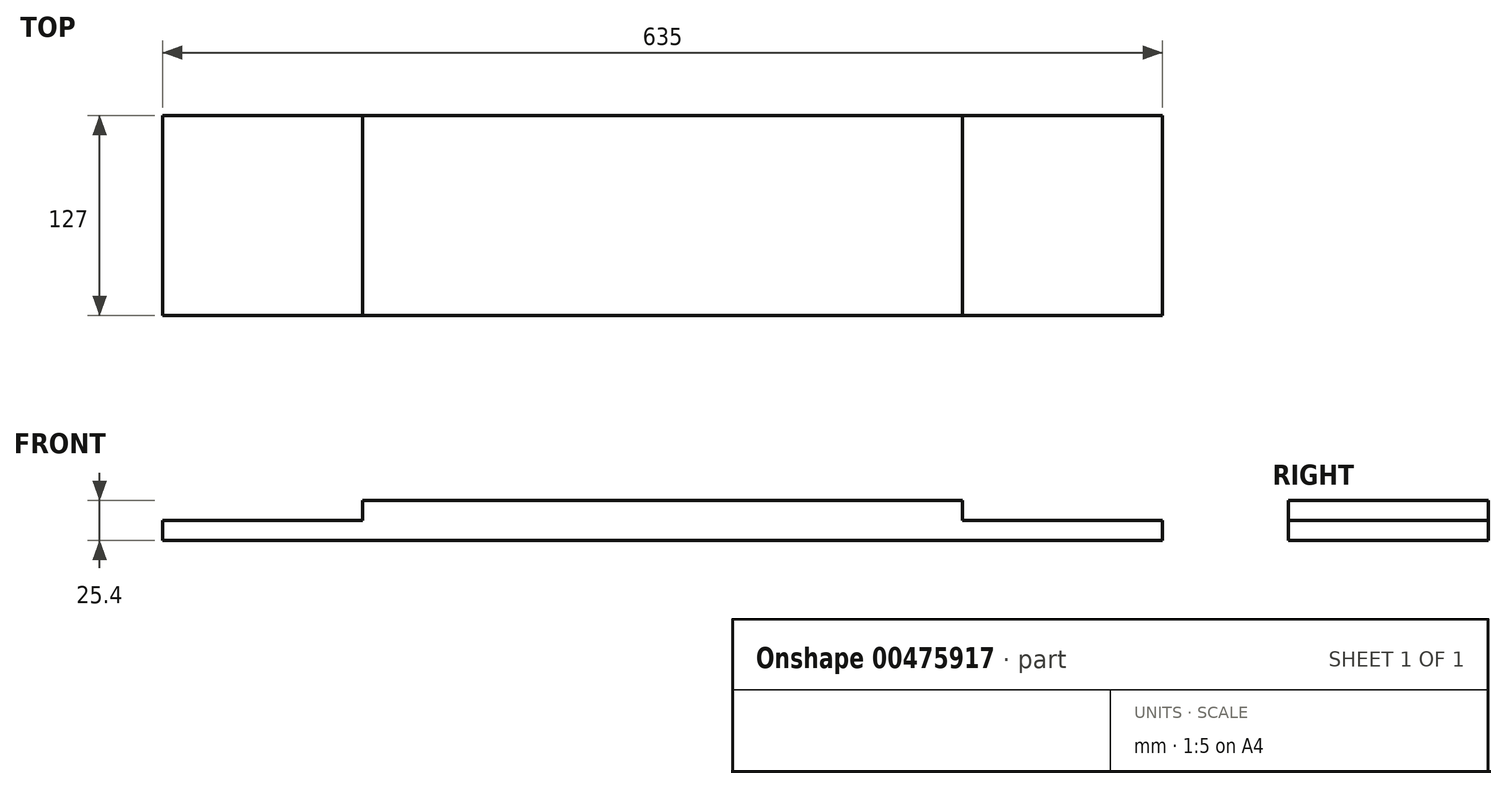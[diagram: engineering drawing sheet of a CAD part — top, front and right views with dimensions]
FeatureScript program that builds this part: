
annotation { "Feature Type Name" : "Feature", "Feature Type Description" : "" }
export const myFeature = defineFeature(function(context is Context, id is Id, definition is map)
    precondition{}
    {
        {
            var Q0;
            Q0=qCreatedBy(makeId("Top.planeOp"),FACE);
            var sketch = newSketch(context, id + "F0", { "sketchPlane" : qUnion([Q0])});
            skLineSegment(sketch, "E0.bottom", {"start": v(-183.86, -84.48) * mm, "end": v(197.14, -84.48) * mm});
            skLineSegment(sketch, "E0.top", {"start": v(-183.86, 42.52) * mm, "end": v(197.14, 42.52) * mm});
            skLineSegment(sketch, "E0.left", {"start": v(-183.86, -84.48) * mm, "end": v(-183.86, 42.52) * mm});
            skLineSegment(sketch, "E0.right", {"start": v(197.14, -84.48) * mm, "end": v(197.14, 42.52) * mm});
            skSolve(sketch);
        }
        {
            var Q0;
            Q0 = qSketchRegion(id + "F0", true);
            extrude(context, id + "F1", {"entities" : qUnion([Q0]), "depth" : 12.7 * mm, "offsetDistance" : 25.4 * mm});
        }
        {
            var Q0;
            Q0=makeQuery(id+"F1.opExtrude","CAP_FACE",FACE,{"disambiguationData":[OSD([sQuery(id+"F0.wireOp",EDGE,"E0.bottom"),sQuery(id+"F0.wireOp",EDGE,"E0.top"),sQuery(id+"F0.wireOp",EDGE,"E0.left"),sQuery(id+"F0.wireOp",EDGE,"E0.right")])],"isStart":true});
            var sketch = newSketch(context, id + "F2", { "sketchPlane" : qUnion([Q0])});
            skLineSegment(sketch, "E1.bottom", {"start": v(-310.86, -42.52) * mm, "end": v(324.14, -42.52) * mm});
            skLineSegment(sketch, "E1.top", {"start": v(-310.86, 84.48) * mm, "end": v(324.14, 84.48) * mm});
            skLineSegment(sketch, "E1.left", {"start": v(-310.86, -42.52) * mm, "end": v(-310.86, 84.48) * mm});
            skLineSegment(sketch, "E1.right", {"start": v(324.14, -42.52) * mm, "end": v(324.14, 84.48) * mm});
            skSolve(sketch);
        }
        {
            var Q0;
            Q0 = qSketchRegion(id + "F2", true);
            extrude(context, id + "F3", {"entities" : qUnion([Q0]), "operationType" : NewBodyOperationType.ADD, "depth" : 12.7 * mm, "offsetDistance" : 25.4 * mm});
        }
    });
